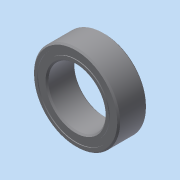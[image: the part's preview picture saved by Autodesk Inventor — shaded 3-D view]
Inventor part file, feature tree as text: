
AUTODESK INVENTOR PART (.ipt)
format: ipt  version: 2015 (Build 190159000, 159)  size: 593,920 bytes
history: native  units: in
note: dims shown in document units (in); Inventor stores cm internally (conversion verified against a paired STEP export)
features: imported_body x16, other x12, revolve x5
ambient origin geometry x8: Origin, YZ Plane, XZ Plane, XY Plane, X Axis, Y Axis, Z Axis, Center Point
bodies: Body1 (feature_tree), Body2 (feature_tree), Body3 (feature_tree), Body4 (feature_tree), Body5 (feature_tree), Body6 (feature_tree), Body7 (feature_tree), Body8 (feature_tree), Body9 (feature_tree), Body10 (feature_tree), Body11 (feature_tree), Body12 (feature_tree), Body13 (feature_tree), Body14 (feature_tree), Body15 (feature_tree), Body16 (feature_tree)
feature tree (33):
  revolve  "Revolve1"  [1 undecoded]
  other  "57155K3751"
  revolve  "Revolve3"  [1 undecoded]
  revolve  "Revolve4"  [1 undecoded]
  other  "CirPattern1[1]"
  other  "CirPattern1[2]"
  other  "CirPattern1[3]"
  other  "CirPattern1[4]"
  other  "CirPattern1[5]"
  other  "CirPattern1[6]"
  other  "CirPattern1[7]"
  other  "CirPattern1[8]"
  other  "CirPattern1[9]"
  other  "CirPattern1[10]"
  other  "CirPattern1[11]"
  revolve  "Revolve5[1]"  [1 undecoded]
  revolve  "Revolve5[2]"  [1 undecoded]
  imported_body  "Base1"
  imported_body  "Base2"
  imported_body  "Base3"
  imported_body  "Base4"
  imported_body  "Base5"
  imported_body  "Base6"
  imported_body  "Base7"
  imported_body  "Base8"
  imported_body  "Base9"
  imported_body  "Base10"
  imported_body  "Base11"
  imported_body  "Base12"
  imported_body  "Base13"
  imported_body  "Base14"
  imported_body  "Base15"
  imported_body  "Base16"
note: 5 required parameter values undecoded (feature->parameter linkage not recoverable at this tier; creation-order binding heuristic only, values carry confidence <= 0.55)
